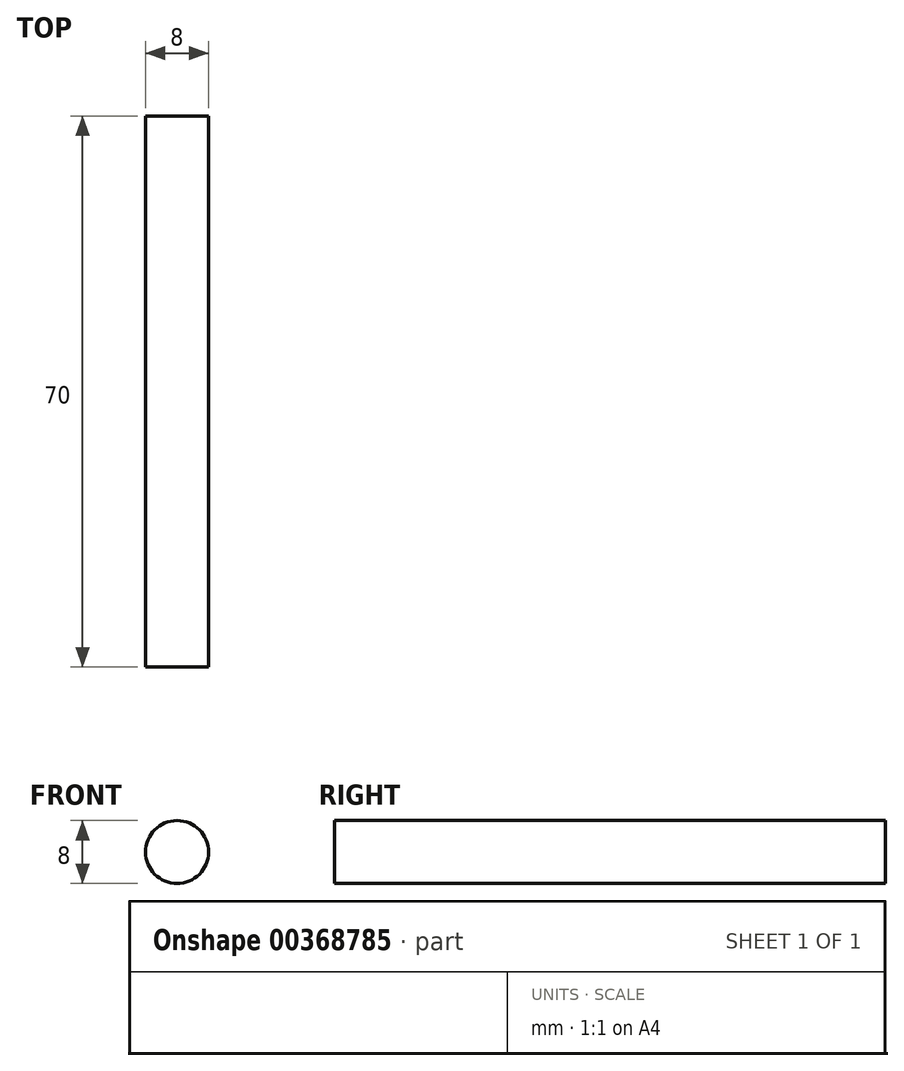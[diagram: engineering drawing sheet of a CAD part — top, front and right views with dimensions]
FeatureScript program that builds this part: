
annotation { "Feature Type Name" : "Feature", "Feature Type Description" : "" }
export const myFeature = defineFeature(function(context is Context, id is Id, definition is map)
    precondition{}
    {
        {
            var Q0;
            Q0=qCreatedBy(makeId("Front.planeOp"),FACE);
            var sketch = newSketch(context, id + "F0", { "sketchPlane" : qUnion([Q0])});
            skCircle(sketch, "E0", {"center": v(0, 0) * mm, "radius": 4 * mm});
            skSolve(sketch);
        }
        {
            var Q0;
            Q0 = qSketchRegion(id + "F0", true);
            extrude(context, id + "F1", {"entities" : qUnion([Q0]), "depth" : 70 * mm});
        }
    });
